# Revit family: Quick_Coupling-Grohe-64999
name_source: partatom
category: Plumbing Fixtures
units: mm (PartAtom-declared; Revit-internal decimal feet)

## family parameters
Always vertical = No
Cut with Voids When Loaded = No
OmniClass Number = 23.60.30.11.14
OmniClass Title = Pipework Fittings
Part Type = Normal
Room Calculation Point = No
Round Connector Dimension = Use Diameter
Shared = Yes
Work Plane-Based = Yes

## types (1)
- 64999
    Assembly Code = D2040100
    CW Connection = No
    Default Elevation = 0"
    Description = Universal Quick Coupling
    Finish = Plastic-Grohe-Black
    Flow Rate = 1.5 gpm
    HW Connection = No
    Height = 2 1/2"
    Length = 1"
    Manufacturer = Grohe
    Material = Plastic-Grohe-Black
    Model = 64999
    Price = Prices may vary. Please consult Manufacturer Representative for most up-to-date price list.
    Product Page URL = https://www.grohe.us
    Tempered Water Connection = Yes
    Tempered Water Connection Diameter = 1"
    Tempered Water Connection Radius = 1/2"
    URL = https://www.grohe.us
    Vent Connection = No
    Waste Connection = No
    Width = 1"

## geometry (parser evidence)
native form markers: Sweep x2
no freeform markers — native parametric forms only
